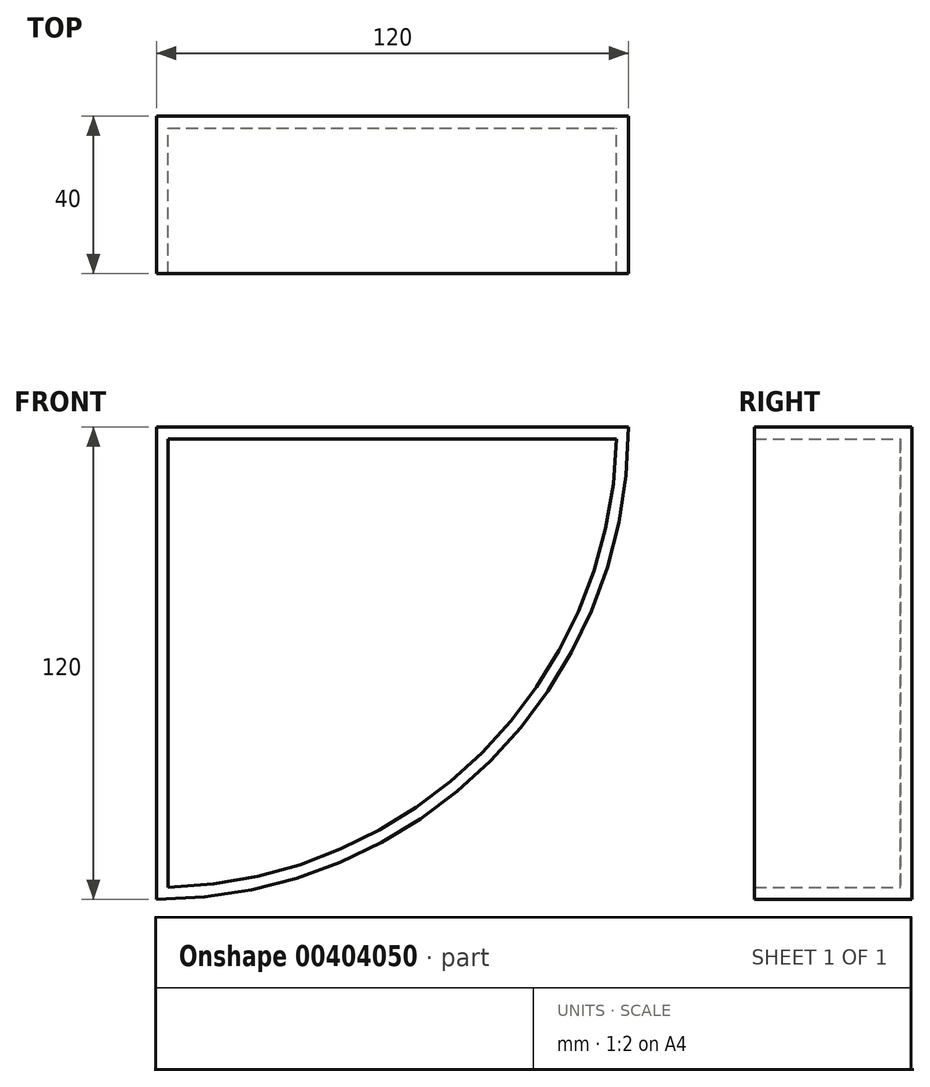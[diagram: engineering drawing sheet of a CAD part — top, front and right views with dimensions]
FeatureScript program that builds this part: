
annotation { "Feature Type Name" : "Feature", "Feature Type Description" : "" }
export const myFeature = defineFeature(function(context is Context, id is Id, definition is map)
    precondition{}
    {
        {
            var Q0;
            Q0=qCreatedBy(makeId("Front.planeOp"),FACE);
            var sketch = newSketch(context, id + "F0", { "sketchPlane" : qUnion([Q0])});
            skArc(sketch, "E0", {"start": v(0, -119.91) * mm, "mid": v(84.85, -84.77) * mm, "end": v(120, 0.09) * mm});
            skLineSegment(sketch, "E1", {"start": v(0, 0.09) * mm, "end": v(120, 0.09) * mm});
            skLineSegment(sketch, "E2", {"start": v(0, 0.09) * mm, "end": v(0, -119.91) * mm});
            skSolve(sketch);
        }
        {
            var Q0;
            Q0=makeQuery(id+"F0.imprint","IMPRINT",FACE,{"disambiguationData":[TD([[makeQuery(id+"F0.imprint","IMPRINT",EDGE,{"derivedFrom":sQuery(id+"F0.wireOp",EDGE,"E0")}),1.0]])]});
            extrude(context, id + "F1", {"entities" : qUnion([Q0]), "depth" : 40 * mm});
        }
        {
            var Q0;
            Q0=makeQuery(id+"F1.opExtrude","CAP_FACE",FACE,{"disambiguationData":[OSD([sQuery(id+"F0.wireOp",EDGE,"E0"),sQuery(id+"F0.wireOp",EDGE,"E1"),sQuery(id+"F0.wireOp",EDGE,"E2")])],"isStart":false});
            shell(context, id + "F2", {"entities" : qUnion([Q0]), "thickness" : 3 * mm});
        }
    });
